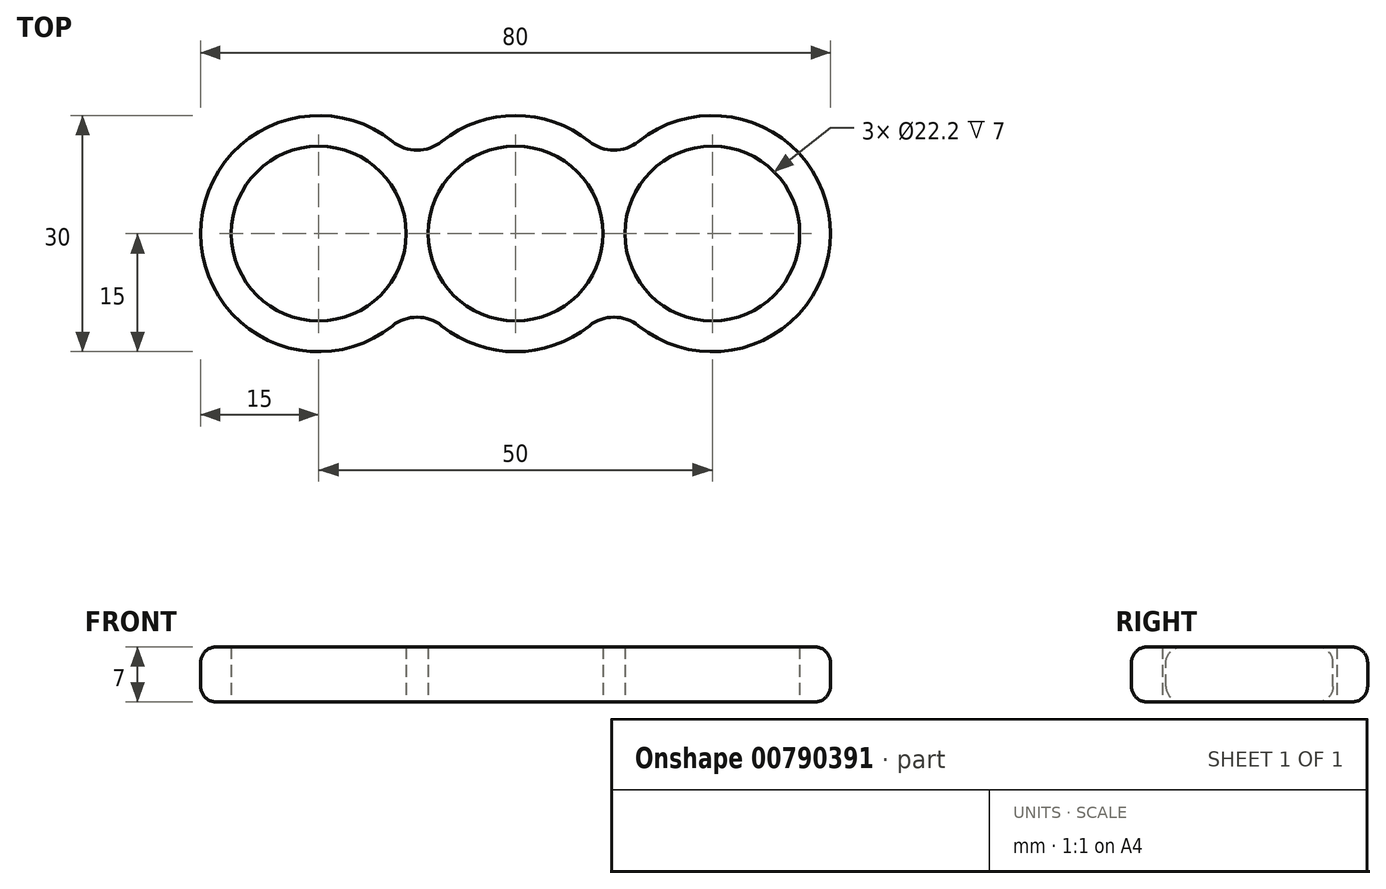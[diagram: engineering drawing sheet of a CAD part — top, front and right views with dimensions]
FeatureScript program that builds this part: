
annotation { "Feature Type Name" : "Feature", "Feature Type Description" : "" }
export const myFeature = defineFeature(function(context is Context, id is Id, definition is map)
    precondition{}
    {
        {
            var Q0;
            Q0=qCreatedBy(makeId("Top.planeOp"),FACE);
            var sketch = newSketch(context, id + "F0", { "sketchPlane" : qUnion([Q0])});
            skArc(sketch, "E0", {"start": v(-12.5, 8.3) * mm, "mid": v(-40, 0) * mm, "end": v(-12.5, -8.3) * mm});
            skArc(sketch, "E1", {"start": v(12.5, -8.3) * mm, "mid": v(40, 0) * mm, "end": v(12.5, 8.3) * mm});
            skCircle(sketch, "E2", {"center": v(25, 0) * mm, "radius": 11.1 * mm});
            skCircle(sketch, "E3", {"center": v(-25, 0) * mm, "radius": 11.1 * mm});
            skCircle(sketch, "E4", {"center": v(0, 0) * mm, "radius": 11.1 * mm});
            skArc(sketch, "E5", {"start": v(-12.5, -8.3) * mm, "mid": v(0, -15) * mm, "end": v(12.5, -8.3) * mm});
            skArc(sketch, "E6.trimOffspring", {"start": v(12.5, 8.3) * mm, "mid": v(0, 15) * mm, "end": v(-12.5, 8.3) * mm});
            skSolve(sketch);
        }
        {
            var Q0;
            Q0=makeQuery(id+"F0.imprint","IMPRINT",FACE,{"disambiguationData":[TD([[makeQuery(id+"F0.imprint","IMPRINT",EDGE,{"derivedFrom":sQuery(id+"F0.wireOp",EDGE,"E0")}),1.0]])]});
            extrude(context, id + "F1", {"entities" : qUnion([Q0]), "depth" : 7 * mm, "offsetDistance" : 25 * mm});
        }
        {
            var Q0;
            Q0=makeQuery(id+"F1.opExtrude","SWEPT_EDGE",EDGE,{"disambiguationData":[OSD([sQuery(id+"F0.wireOp",EDGE,"E0"),sQuery(id+"F0.wireOp",EDGE,"E5")])]});
            var Q1;
            Q1=makeQuery(id+"F1.opExtrude","SWEPT_EDGE",EDGE,{"disambiguationData":[OSD([sQuery(id+"F0.wireOp",EDGE,"E1"),sQuery(id+"F0.wireOp",EDGE,"E5")])]});
            var Q2;
            Q2=makeQuery(id+"F1.opExtrude","SWEPT_EDGE",EDGE,{"disambiguationData":[OSD([sQuery(id+"F0.wireOp",EDGE,"E1"),sQuery(id+"F0.wireOp",EDGE,"E6.trimOffspring")])]});
            var Q3;
            Q3=makeQuery(id+"F1.opExtrude","SWEPT_EDGE",EDGE,{"disambiguationData":[OSD([sQuery(id+"F0.wireOp",EDGE,"E0"),sQuery(id+"F0.wireOp",EDGE,"E6.trimOffspring")])]});
            fillet(context, id + "F2", {"entities" : qUnion([Q0, Q1, Q2, Q3]), "radius" : 5 * mm, "tangentPropagation" : true, "allowEdgeOverflow" : false});
        }
        {
            var Q0;
            Q0=makeQuery(id+"F1.opExtrude","CAP_EDGE",EDGE,{"disambiguationData":[OSD([sQuery(id+"F0.wireOp",EDGE,"E0")])],"isStart":false});
            var Q1;
            Q1=makeQuery(id+"F1.opExtrude","CAP_EDGE",EDGE,{"disambiguationData":[OSD([sQuery(id+"F0.wireOp",EDGE,"E0")])],"isStart":true});
            fillet(context, id + "F3", {"entities" : qUnion([Q0, Q1]), "radius" : 2 * mm, "tangentPropagation" : true, "allowEdgeOverflow" : false});
        }
    });
